# Revit family: OO313CC
name_source: partatom
category: Apparecchi idraulici
units: mm (PartAtom-declared; Revit-internal decimal feet)

## family parameters
Basato su piano di lavoro = No
Condiviso = No
Mantieni orientamento annotazione = No
Numero OmniClass = 23.45.55.17
Punto di calcolo locali = No
Quota connettore circolare = Usa diametro
Sempre verticale = Sì
Taglio con vuoti quando caricato = No
Tipo di parte = Normale
Titolo OmniClass = Mixing Faucets

## types (1)
- Chrome
    Commenti sul tipo = Wall mixer
    Connessione CW = No
    Connessione HW = No
    Connessione di scarico = No
    Connessione di ventilazione = No
    Descrizione = Exposed parts for manual wall mixer with two ways diverter and shower kit
    Finishes surface = IB_Chrome
    Immagine tipo = OO313CC.jpg
    Modello = OO313CC
    Produttore = IB Rubinetterie S.p.A.
    Prospetto di default = 0 mm  [stored 0 ft]
    URL = https://www.weareib.it

note: [stored X ft] marks values corroborated as IEEE doubles in the binary element streams (Revit-internal decimal feet)
